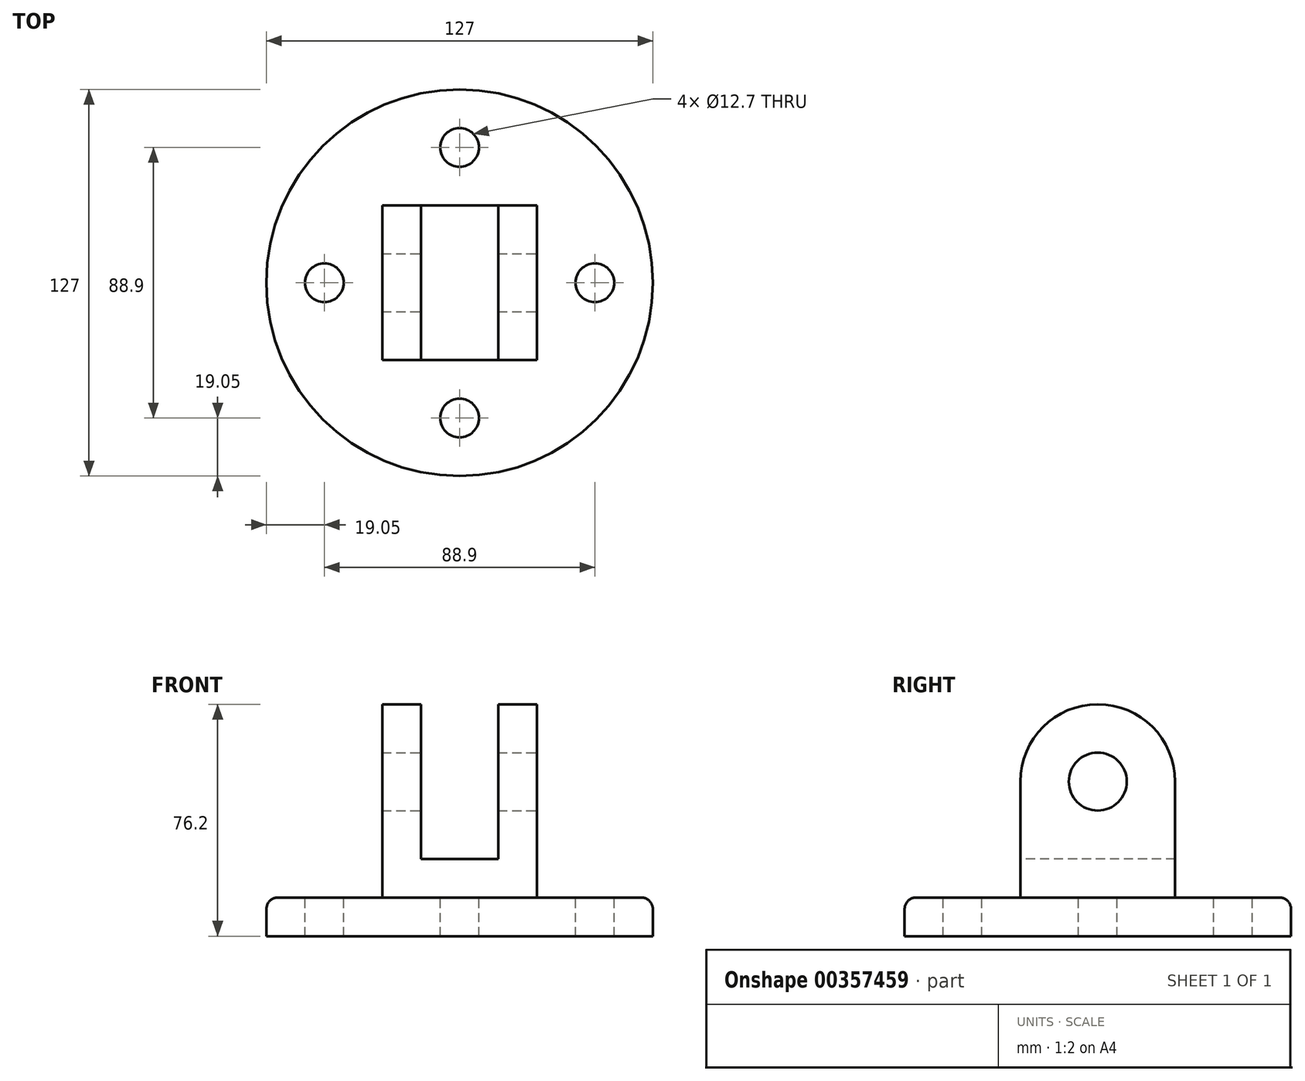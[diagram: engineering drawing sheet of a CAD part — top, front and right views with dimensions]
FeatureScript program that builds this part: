
annotation { "Feature Type Name" : "Feature", "Feature Type Description" : "" }
export const myFeature = defineFeature(function(context is Context, id is Id, definition is map)
    precondition{}
    {
        {
            var Q0;
            Q0=qCreatedBy(makeId("Top.planeOp"),FACE);
            var sketch = newSketch(context, id + "F0", { "sketchPlane" : qUnion([Q0])});
            skCircle(sketch, "E0", {"center": v(0, 0) * mm, "radius": 63.5 * mm});
            skSolve(sketch);
        }
        {
            var Q0;
            Q0 = qSketchRegion(id + "F0", true);
            extrude(context, id + "F1", {"entities" : qUnion([Q0]), "endBound" : BoundingType.SYMMETRIC, "depth" : 12.7 * mm});
        }
        {
            var Q0;
            Q0=makeQuery(id+"F1.opExtrude","CAP_FACE",FACE,{"disambiguationData":[OSD([sQuery(id+"F0.wireOp",EDGE,"E0")])],"isStart":false});
            var sketch = newSketch(context, id + "F2", { "sketchPlane" : qUnion([Q0])});
            skLineSegment(sketch, "E1", {"start": v(-25.4, 25.4) * mm, "end": v(25.4, 25.4) * mm});
            skLineSegment(sketch, "E2", {"start": v(25.4, 25.4) * mm, "end": v(25.4, -25.4) * mm});
            skLineSegment(sketch, "E3", {"start": v(25.4, -25.4) * mm, "end": v(-25.4, -25.4) * mm});
            skLineSegment(sketch, "E4", {"start": v(-25.4, 25.4) * mm, "end": v(-25.4, -25.4) * mm});
            skSolve(sketch);
        }
        {
            var Q0;
            Q0 = qSketchRegion(id + "F2", true);
            extrude(context, id + "F3", {"entities" : qUnion([Q0]), "operationType" : NewBodyOperationType.ADD, "depth" : 76.2 * mm});
        }
        {
            var Q0;
            Q0=makeQuery(id+"F3.opExtrude","SWEPT_FACE",FACE,{"disambiguationData":[OSD([sQuery(id+"F2.wireOp",EDGE,"E3")])]});
            var sketch = newSketch(context, id + "F4", { "sketchPlane" : qUnion([Q0])});
            skLineSegment(sketch, "E5", {"start": v(25.4, 6.35) * mm, "end": v(-25.4, 6.35) * mm});
            skLineSegment(sketch, "E6", {"start": v(-25.4, 6.35) * mm, "end": v(-25.4, 82.55) * mm});
            skLineSegment(sketch, "E7", {"start": v(-25.4, 82.55) * mm, "end": v(-12.7, 82.55) * mm});
            skLineSegment(sketch, "E8", {"start": v(25.4, 6.35) * mm, "end": v(25.4, 82.55) * mm});
            skLineSegment(sketch, "E9", {"start": v(25.4, 82.55) * mm, "end": v(12.7, 82.55) * mm});
            skLineSegment(sketch, "E10", {"start": v(-12.7, 82.55) * mm, "end": v(-12.7, 19.05) * mm});
            skLineSegment(sketch, "E11", {"start": v(-12.7, 19.05) * mm, "end": v(12.7, 19.05) * mm});
            skLineSegment(sketch, "E12", {"start": v(12.7, 82.55) * mm, "end": v(12.7, 19.05) * mm});
            skLineSegment(sketch, "E13", {"start": v(-12.7, 82.55) * mm, "end": v(12.7, 82.55) * mm});
            skSolve(sketch);
        }
        {
            var Q0;
            Q0=makeQuery(id+"F4.imprint","IMPRINT",FACE,{"disambiguationData":[TD([[makeQuery(id+"F4.imprint","IMPRINT",EDGE,{"derivedFrom":sQuery(id+"F4.wireOp",EDGE,"E10")}),1.0]])]});
            extrude(context, id + "F5", {"entities" : qUnion([Q0]), "operationType" : NewBodyOperationType.REMOVE, "endBound" : BoundingType.THROUGH_ALL, "oppositeDirection" : true, "depth" : 25.4 * mm});
        }
        {
            var Q0;
            Q0=makeQuery(id+"F3.opExtrude","SWEPT_FACE",FACE,{"disambiguationData":[OSD([sQuery(id+"F2.wireOp",EDGE,"E2")])]});
            var sketch = newSketch(context, id + "F6", { "sketchPlane" : qUnion([Q0])});
            skCircle(sketch, "E14", {"center": v(0, 44.45) * mm, "radius": 9.53 * mm});
            skSolve(sketch);
        }
        {
            var Q0;
            Q0=makeQuery(id+"F6.imprint","IMPRINT",FACE,{"disambiguationData":[TD([[makeQuery(id+"F6.imprint","IMPRINT",EDGE,{"derivedFrom":sQuery(id+"F6.wireOp",EDGE,"E14")}),-1.0]])]});
            var sketch = newSketch(context, id + "F7", { "sketchPlane" : qUnion([Q0])});
            skArc(sketch, "E15", {"start": v(25.4, 44.45) * mm, "mid": v(0, 69.85) * mm, "end": v(-25.4, 44.45) * mm});
            skLineSegment(sketch, "E16", {"start": v(-25.4, 44.45) * mm, "end": v(-25.4, 82.55) * mm});
            skLineSegment(sketch, "E17", {"start": v(-25.4, 82.55) * mm, "end": v(25.4, 82.55) * mm});
            skLineSegment(sketch, "E18", {"start": v(25.4, 82.55) * mm, "end": v(25.4, 44.45) * mm});
            skSolve(sketch);
        }
        {
            var Q0;
            Q0=makeQuery(id+"F6.imprint","IMPRINT",FACE,{"disambiguationData":[TD([[makeQuery(id+"F6.imprint","IMPRINT",EDGE,{"derivedFrom":sQuery(id+"F6.wireOp",EDGE,"E14")}),1.0]])]});
            extrude(context, id + "F8", {"entities" : qUnion([Q0]), "operationType" : NewBodyOperationType.REMOVE, "endBound" : BoundingType.THROUGH_ALL, "oppositeDirection" : true, "depth" : 25.4 * mm});
        }
        {
            var Q0;
            Q0=makeQuery(id+"F7.imprint","IMPRINT",FACE,{"disambiguationData":[TD([[makeQuery(id+"F7.imprint","IMPRINT",EDGE,{"derivedFrom":sQuery(id+"F7.wireOp",EDGE,"E15")}),-1.0]])]});
            extrude(context, id + "F9", {"entities" : qUnion([Q0]), "operationType" : NewBodyOperationType.REMOVE, "endBound" : BoundingType.THROUGH_ALL, "oppositeDirection" : true, "depth" : 25.4 * mm});
        }
        {
            var Q0;
            Q0=makeQuery(id+"F1.opExtrude","CAP_FACE",FACE,{"disambiguationData":[OSD([sQuery(id+"F0.wireOp",EDGE,"E0")])],"isStart":false});
            var sketch = newSketch(context, id + "F10", { "sketchPlane" : qUnion([Q0])});
            skCircle(sketch, "E19", {"center": v(0, 0) * mm, "radius": 44.45 * mm});
            skPoint(sketch, "E20.endSnap0", {"position": v(25.4, 0) * mm});
            skCircle(sketch, "E21", {"center": v(0, 44.45) * mm, "radius": 6.35 * mm});
            skCircle(sketch, "E22", {"center": v(0, -44.45) * mm, "radius": 6.35 * mm});
            skCircle(sketch, "E23", {"center": v(44.45, 0) * mm, "radius": 6.35 * mm});
            skCircle(sketch, "E24", {"center": v(-44.45, 0) * mm, "radius": 6.35 * mm});
            skPoint(sketch, "E24.centerSnap0", {"position": v(-25.4, 0) * mm});
            skSolve(sketch);
        }
        {
            var Q0;
            {var subQ0=sQuery(id+"F10.wireOp",EDGE,"E24");var subQ1=sQuery(id+"F10.wireOp",EDGE,"E19");var subQ2=makeQuery(id+"F10.imprint","INTERSECT",VERTEX,{"disambiguationData":[OD(0.0)],"derivedFrom":[subQ1,subQ0]});Q0=makeQuery(id+"F10.imprint","IMPRINT",FACE,{"disambiguationData":[TD([[makeQuery(id+"F10.imprint","IMPRINT",EDGE,{"disambiguationData":[TD([[subQ2,-1.0]])],"derivedFrom":subQ1}),-1.0]])]});}
            var Q1;
            {var subQ0=sQuery(id+"F10.wireOp",EDGE,"E24");var subQ1=sQuery(id+"F10.wireOp",EDGE,"E19");var subQ2=makeQuery(id+"F10.imprint","INTERSECT",VERTEX,{"disambiguationData":[OD(0.0)],"derivedFrom":[subQ1,subQ0]});Q1=makeQuery(id+"F10.imprint","IMPRINT",FACE,{"disambiguationData":[TD([[makeQuery(id+"F10.imprint","IMPRINT",EDGE,{"disambiguationData":[TD([[subQ2,-1.0]])],"derivedFrom":subQ1}),1.0]])]});}
            var Q2;
            {var subQ0=sQuery(id+"F10.wireOp",EDGE,"E21");var subQ1=sQuery(id+"F10.wireOp",EDGE,"E19");var subQ2=makeQuery(id+"F10.imprint","INTERSECT",VERTEX,{"disambiguationData":[OD(0.0)],"derivedFrom":[subQ1,subQ0]});Q2=makeQuery(id+"F10.imprint","IMPRINT",FACE,{"disambiguationData":[TD([[makeQuery(id+"F10.imprint","IMPRINT",EDGE,{"disambiguationData":[TD([[subQ2,-1.0]])],"derivedFrom":subQ1}),1.0]])]});}
            var Q3;
            {var subQ0=sQuery(id+"F10.wireOp",EDGE,"E21");var subQ1=sQuery(id+"F10.wireOp",EDGE,"E19");var subQ2=makeQuery(id+"F10.imprint","INTERSECT",VERTEX,{"disambiguationData":[OD(0.0)],"derivedFrom":[subQ1,subQ0]});Q3=makeQuery(id+"F10.imprint","IMPRINT",FACE,{"disambiguationData":[TD([[makeQuery(id+"F10.imprint","IMPRINT",EDGE,{"disambiguationData":[TD([[subQ2,-1.0]])],"derivedFrom":subQ1}),-1.0]])]});}
            var Q4;
            {var subQ0=sQuery(id+"F10.wireOp",EDGE,"E23");var subQ1=sQuery(id+"F10.wireOp",EDGE,"E19");var subQ2=makeQuery(id+"F10.imprint","INTERSECT",VERTEX,{"disambiguationData":[OD(0.0)],"derivedFrom":[subQ1,subQ0]});Q4=makeQuery(id+"F10.imprint","IMPRINT",FACE,{"disambiguationData":[TD([[makeQuery(id+"F10.imprint","IMPRINT",EDGE,{"disambiguationData":[TD([[subQ2,1.0]])],"derivedFrom":subQ1}),1.0]])]});}
            var Q5;
            {var subQ0=sQuery(id+"F10.wireOp",EDGE,"E23");var subQ1=sQuery(id+"F10.wireOp",EDGE,"E19");var subQ2=makeQuery(id+"F10.imprint","INTERSECT",VERTEX,{"disambiguationData":[OD(0.0)],"derivedFrom":[subQ1,subQ0]});Q5=makeQuery(id+"F10.imprint","IMPRINT",FACE,{"disambiguationData":[TD([[makeQuery(id+"F10.imprint","IMPRINT",EDGE,{"disambiguationData":[TD([[subQ2,1.0]])],"derivedFrom":subQ1}),-1.0]])]});}
            var Q6;
            {var subQ0=sQuery(id+"F10.wireOp",EDGE,"E22");var subQ1=sQuery(id+"F10.wireOp",EDGE,"E19");var subQ2=makeQuery(id+"F10.imprint","INTERSECT",VERTEX,{"disambiguationData":[OD(0.0)],"derivedFrom":[subQ1,subQ0]});Q6=makeQuery(id+"F10.imprint","IMPRINT",FACE,{"disambiguationData":[TD([[makeQuery(id+"F10.imprint","IMPRINT",EDGE,{"disambiguationData":[TD([[subQ2,-1.0]])],"derivedFrom":subQ1}),1.0]])]});}
            var Q7;
            {var subQ0=sQuery(id+"F10.wireOp",EDGE,"E22");var subQ1=sQuery(id+"F10.wireOp",EDGE,"E19");var subQ2=makeQuery(id+"F10.imprint","INTERSECT",VERTEX,{"disambiguationData":[OD(0.0)],"derivedFrom":[subQ1,subQ0]});Q7=makeQuery(id+"F10.imprint","IMPRINT",FACE,{"disambiguationData":[TD([[makeQuery(id+"F10.imprint","IMPRINT",EDGE,{"disambiguationData":[TD([[subQ2,-1.0]])],"derivedFrom":subQ1}),-1.0]])]});}
            extrude(context, id + "F11", {"entities" : qUnion([Q0, Q1, Q2, Q3, Q4, Q5, Q6, Q7]), "operationType" : NewBodyOperationType.REMOVE, "endBound" : BoundingType.THROUGH_ALL, "oppositeDirection" : true, "depth" : 25.4 * mm});
        }
        {
            var Q0;
            Q0=makeQuery(id+"F1.opExtrude","CAP_EDGE",EDGE,{"disambiguationData":[OSD([sQuery(id+"F0.wireOp",EDGE,"E0")])],"isStart":false});
            var Q1;
            Q1=makeQuery(id+"F3.opExtrude","CAP_EDGE",EDGE,{"disambiguationData":[OSD([sQuery(id+"F2.wireOp",EDGE,"E2")])],"isStart":true});
            var Q2;
            Q2=makeQuery(id+"F3.opExtrude","CAP_EDGE",EDGE,{"disambiguationData":[OSD([sQuery(id+"F2.wireOp",EDGE,"E3")])],"isStart":true});
            var Q3;
            Q3=makeQuery(id+"F3.opExtrude","CAP_EDGE",EDGE,{"disambiguationData":[OSD([sQuery(id+"F2.wireOp",EDGE,"E4")])],"isStart":true});
            var Q4;
            Q4=makeQuery(id+"F3.opExtrude","CAP_EDGE",EDGE,{"disambiguationData":[OSD([sQuery(id+"F2.wireOp",EDGE,"E1")])],"isStart":true});
            fillet(context, id + "F12", {"entities" : qUnion([Q0, Q1, Q2, Q3, Q4]), "radius" : 3.8 * mm, "tangentPropagation" : true, "allowEdgeOverflow" : false});
        }
    });
